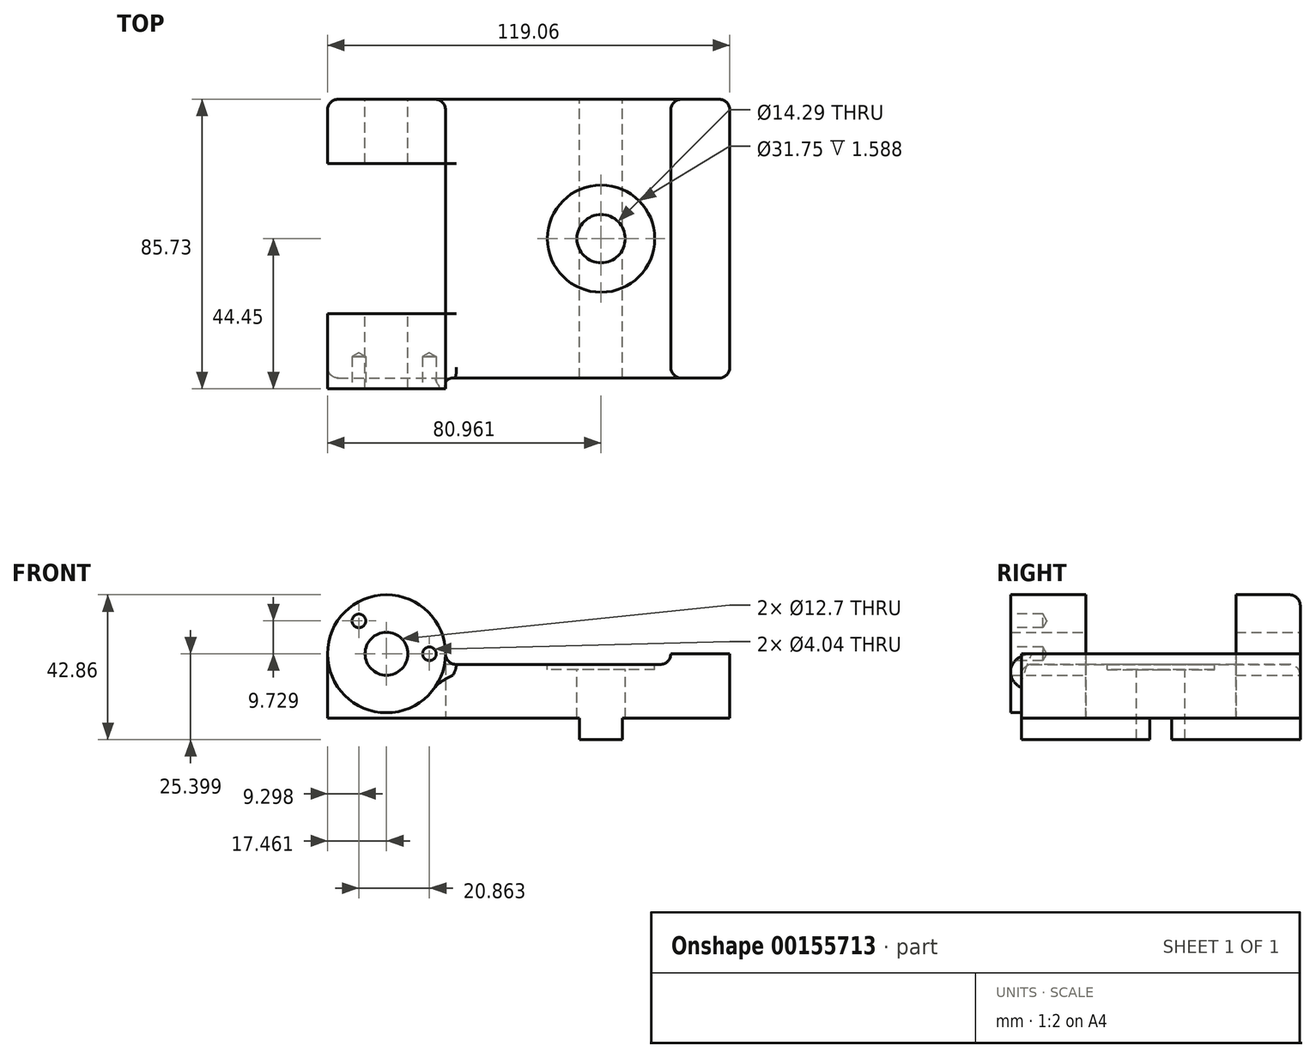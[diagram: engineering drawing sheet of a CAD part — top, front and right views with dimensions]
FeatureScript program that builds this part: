
annotation { "Feature Type Name" : "Feature", "Feature Type Description" : "" }
export const myFeature = defineFeature(function(context is Context, id is Id, definition is map)
    precondition{}
    {
        {
            var Q0;
            Q0=qCreatedBy(makeId("Front.planeOp"),FACE);
            var sketch = newSketch(context, id + "F0", { "sketchPlane" : qUnion([Q0])});
            skLineSegment(sketch, "E0", {"start": v(-59.53, -15.08) * mm, "end": v(15.08, -15.08) * mm});
            skLineSegment(sketch, "E1", {"start": v(15.08, -15.08) * mm, "end": v(15.08, -21.43) * mm});
            skLineSegment(sketch, "E2", {"start": v(15.08, -21.43) * mm, "end": v(27.78, -21.43) * mm});
            skLineSegment(sketch, "E3", {"start": v(27.78, -21.43) * mm, "end": v(27.78, -15.08) * mm});
            skLineSegment(sketch, "E4", {"start": v(27.78, -15.08) * mm, "end": v(59.53, -15.08) * mm});
            skLineSegment(sketch, "E5", {"start": v(59.53, -15.08) * mm, "end": v(59.53, 3.97) * mm});
            skLineSegment(sketch, "E6", {"start": v(59.53, 3.97) * mm, "end": v(42.07, 3.97) * mm});
            skLineSegment(sketch, "E7", {"start": v(42.07, 3.97) * mm, "end": v(42.07, 0.8) * mm});
            skLineSegment(sketch, "E8", {"start": v(42.07, 0.8) * mm, "end": v(-24.9, 0.8) * mm});
            skLineSegment(sketch, "E9", {"start": v(-59.53, -15.08) * mm, "end": v(-59.53, 3.97) * mm});
            skLineSegment(sketch, "E10", {"start": v(0, 21.43) * mm, "end": v(0, -21.43) * mm, "construction": true});
            skCircle(sketch, "E11", {"center": v(-42.07, 3.97) * mm, "radius": 6.35 * mm});
            skArc(sketch, "E12", {"start": v(-24.9, 0.8) * mm, "mid": v(-40.47, 21.36) * mm, "end": v(-59.53, 3.97) * mm});
            skPoint(sketch, "E13", {"position": v(-42.07, 21.43) * mm});
            skSolve(sketch);
        }
        {
            var Q0;
            Q0 = qSketchRegion(id + "F0", true);
            extrude(context, id + "F1", {"entities" : qUnion([Q0]), "endBound" : BoundingType.SYMMETRIC, "depth" : 82.55 * mm});
        }
        {
            var Q0;
            Q0=makeQuery(id+"F1.opExtrude","CAP_FACE",FACE,{"disambiguationData":[OSD([sQuery(id+"F0.wireOp",EDGE,"E0"),sQuery(id+"F0.wireOp",EDGE,"E1"),sQuery(id+"F0.wireOp",EDGE,"E2"),sQuery(id+"F0.wireOp",EDGE,"E3"),sQuery(id+"F0.wireOp",EDGE,"E4"),sQuery(id+"F0.wireOp",EDGE,"E5"),sQuery(id+"F0.wireOp",EDGE,"E6"),sQuery(id+"F0.wireOp",EDGE,"E7"),sQuery(id+"F0.wireOp",EDGE,"E8"),sQuery(id+"F0.wireOp",EDGE,"E9"),sQuery(id+"F0.wireOp",EDGE,"E11"),sQuery(id+"F0.wireOp",EDGE,"E12")])],"isStart":false});
            var sketch = newSketch(context, id + "F2", { "sketchPlane" : qUnion([Q0])});
            skCircle(sketch, "E14", {"center": v(-42.07, 3.97) * mm, "radius": 17.46 * mm});
            skCircle(sketch, "E15", {"center": v(-42.07, 3.97) * mm, "radius": 6.35 * mm});
            skSolve(sketch);
        }
        {
            var Q0;
            Q0 = qSketchRegion(id + "F2", true);
            extrude(context, id + "F3", {"entities" : qUnion([Q0]), "operationType" : NewBodyOperationType.ADD, "depth" : 3.17 * mm});
        }
        {
            var Q0;
            Q0=makeQuery(id+"F1.opExtrude","SWEPT_FACE",FACE,{"disambiguationData":[OSD([sQuery(id+"F0.wireOp",EDGE,"E8")])]});
            var sketch = newSketch(context, id + "F4", { "sketchPlane" : qUnion([Q0])});
            skPoint(sketch, "E16", {"position": v(21.43, 0) * mm});
            skSolve(sketch);
        }
        {
            var Q0;
            Q0=sQuery(id+"F4.wireOp",VERTEX,"E16");
            var Q1;
            Q1=makeQuery(id+"F1.opExtrude","SWEPT_BODY",BODY,{"disambiguationData":[OSD([sQuery(id+"F0.wireOp",EDGE,"E0"),sQuery(id+"F0.wireOp",EDGE,"E1"),sQuery(id+"F0.wireOp",EDGE,"E2"),sQuery(id+"F0.wireOp",EDGE,"E3"),sQuery(id+"F0.wireOp",EDGE,"E4"),sQuery(id+"F0.wireOp",EDGE,"E5"),sQuery(id+"F0.wireOp",EDGE,"E6"),sQuery(id+"F0.wireOp",EDGE,"E7"),sQuery(id+"F0.wireOp",EDGE,"E8"),sQuery(id+"F0.wireOp",EDGE,"E9"),sQuery(id+"F0.wireOp",EDGE,"E11"),sQuery(id+"F0.wireOp",EDGE,"E12")])]});
            hole(context, id + "F5", {"style" : HoleStyle.C_BORE, "endStyle" : HoleEndStyle.THROUGH, "holeDiameter" : 14.29 * mm, "cBoreDiameter" : 31.75 * mm, "cBoreDepth" : 1.59 * mm, "startFromSketch" : true, "locations" : qUnion([Q0]), "scope" : qUnion([Q1]), "isTappedThrough" : true});
        }
        {
            var Q0;
            Q0=makeQuery(id+"F3.opExtrude","CAP_FACE",FACE,{"disambiguationData":[OSD([sQuery(id+"F2.wireOp",EDGE,"E14"),sQuery(id+"F2.wireOp",EDGE,"E15")])],"isStart":false});
            var sketch = newSketch(context, id + "F6", { "sketchPlane" : qUnion([Q0])});
            skCircle(sketch, "E17", {"center": v(-42.07, 3.97) * mm, "radius": 12.7 * mm, "construction": true});
            skPoint(sketch, "E18", {"position": v(-29.37, 3.97) * mm});
            skLineSegment(sketch, "E19", {"start": v(-42.07, 3.97) * mm, "end": v(-42.07, 16.67) * mm, "construction": true});
            skLineSegment(sketch, "E20", {"start": v(-42.07, 3.97) * mm, "end": v(-50.23, 13.7) * mm, "construction": true});
            skSolve(sketch);
        }
        {
            var Q0;
            Q0=sQuery(id+"F6.wireOp",VERTEX,"E20.end");
            var Q1;
            Q1=sQuery(id+"F6.wireOp",VERTEX,"E18");
            var Q2;
            Q2=makeQuery(id+"F1.opExtrude","SWEPT_BODY",BODY,{"disambiguationData":[OSD([sQuery(id+"F0.wireOp",EDGE,"E0"),sQuery(id+"F0.wireOp",EDGE,"E1"),sQuery(id+"F0.wireOp",EDGE,"E2"),sQuery(id+"F0.wireOp",EDGE,"E3"),sQuery(id+"F0.wireOp",EDGE,"E4"),sQuery(id+"F0.wireOp",EDGE,"E5"),sQuery(id+"F0.wireOp",EDGE,"E6"),sQuery(id+"F0.wireOp",EDGE,"E7"),sQuery(id+"F0.wireOp",EDGE,"E8"),sQuery(id+"F0.wireOp",EDGE,"E9"),sQuery(id+"F0.wireOp",EDGE,"E11"),sQuery(id+"F0.wireOp",EDGE,"E12")])]});
            hole(context, id + "F7", {"style" : HoleStyle.SIMPLE, "endStyle" : HoleEndStyle.BLIND, "standardTappedOrClearance" : lookupTablePath({ "standard" : "ANSI", "engagement" : "75%", "pitch" : "32 tpi", "size" : "#10", "type" : "Tapped" }), "standardBlindInLast" : lookupTablePath({ "standard" : "ANSI", "engagement" : "75%", "pitch" : "32 tpi", "size" : "#10", "type" : "Tapped" }), "holeDiameter" : 4.04 * mm, "holeDepth" : 9.52 * mm, "startFromSketch" : true, "locations" : qUnion([Q0, Q1]), "scope" : qUnion([Q2]), "majorDiameter" : 4.83 * mm});
        }
        {
            var Q0;
            Q0=makeQuery(id+"F1.opExtrude","SWEPT_EDGE",EDGE,{"disambiguationData":[OSD([sQuery(id+"F0.wireOp",EDGE,"E8"),sQuery(id+"F0.wireOp",EDGE,"E12")])]});
            var Q1;
            Q1=makeQuery(id+"F1.opExtrude","CAP_EDGE",EDGE,{"disambiguationData":[OSD([sQuery(id+"F0.wireOp",EDGE,"E8")])],"isStart":false});
            var Q2;
            Q2=makeQuery(id+"F1.opExtrude","SWEPT_EDGE",EDGE,{"disambiguationData":[OSD([sQuery(id+"F0.wireOp",EDGE,"E7"),sQuery(id+"F0.wireOp",EDGE,"E8")])]});
            var Q3;
            Q3=makeQuery(id+"F1.opExtrude","CAP_EDGE",EDGE,{"disambiguationData":[OSD([sQuery(id+"F0.wireOp",EDGE,"E8")])],"isStart":true});
            var Q4;
            Q4=makeQuery(id+"F1.opExtrude","CAP_EDGE",EDGE,{"disambiguationData":[OSD([sQuery(id+"F0.wireOp",EDGE,"E5")])],"isStart":false});
            var Q5;
            Q5=makeQuery(id+"F1.opExtrude","CAP_EDGE",EDGE,{"disambiguationData":[OSD([sQuery(id+"F0.wireOp",EDGE,"E5")])],"isStart":true});
            var Q6;
            Q6=makeQuery(id+"F1.opExtrude","CAP_EDGE",EDGE,{"disambiguationData":[OSD([sQuery(id+"F0.wireOp",EDGE,"E9")])],"isStart":false});
            var Q7;
            Q7=makeQuery(id+"F1.opExtrude","CAP_EDGE",EDGE,{"disambiguationData":[OSD([sQuery(id+"F0.wireOp",EDGE,"E9")])],"isStart":true});
            fillet(context, id + "F8", {"entities" : qUnion([Q0, Q1, Q2, Q3, Q4, Q5, Q6, Q7]), "radius" : 3.17 * mm, "tangentPropagation" : true, "allowEdgeOverflow" : false});
        }
        {
            var Q0;
            Q0=qCreatedBy(makeId("Front.planeOp"),FACE);
            var sketch = newSketch(context, id + "F9", { "sketchPlane" : qUnion([Q0])});
            skLineSegment(sketch, "E21", {"start": v(-59.53, -15.08) * mm, "end": v(-59.53, 21.43) * mm});
            skLineSegment(sketch, "E22", {"start": v(-59.53, 21.43) * mm, "end": v(-21.43, 21.43) * mm});
            skLineSegment(sketch, "E23", {"start": v(-21.43, 21.43) * mm, "end": v(-21.43, 0.8) * mm});
            skLineSegment(sketch, "E24", {"start": v(-21.43, 0.8) * mm, "end": v(-24.6, 0.8) * mm});
            skLineSegment(sketch, "E25", {"start": v(-24.6, 0.8) * mm, "end": v(-24.6, -15.08) * mm});
            skLineSegment(sketch, "E26", {"start": v(-24.6, -15.08) * mm, "end": v(-59.53, -15.08) * mm});
            skSolve(sketch);
        }
        {
            var Q0;
            Q0 = qSketchRegion(id + "F9", true);
            extrude(context, id + "F10", {"entities" : qUnion([Q0]), "operationType" : NewBodyOperationType.REMOVE, "endBound" : BoundingType.SYMMETRIC, "oppositeDirection" : true, "depth" : 44.45 * mm});
        }
    });
